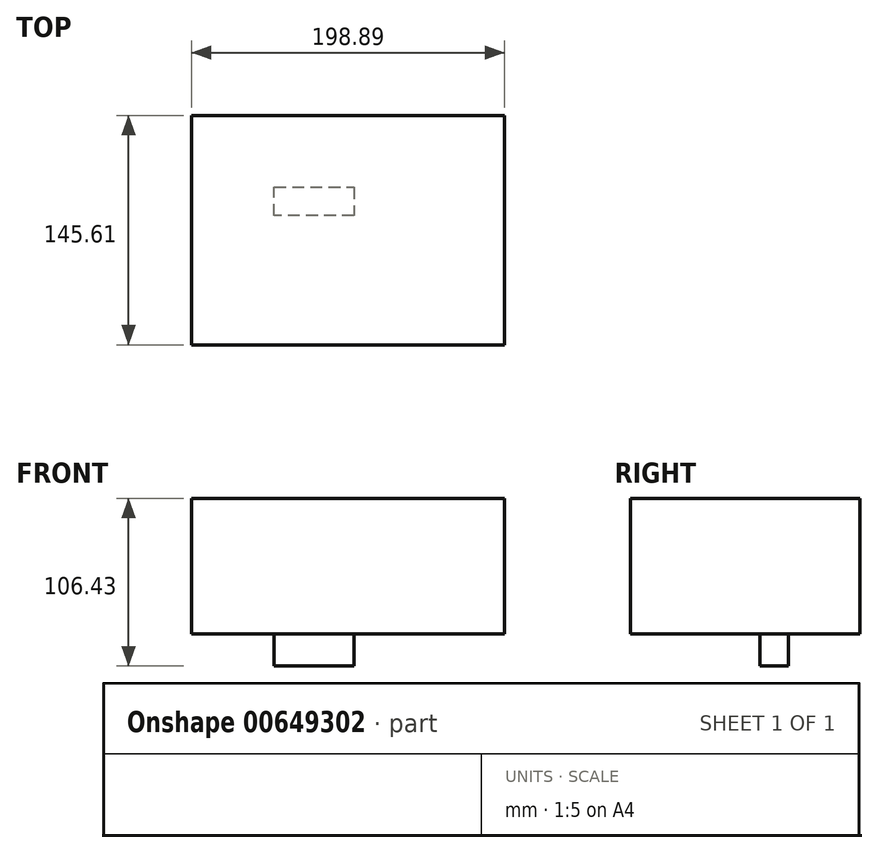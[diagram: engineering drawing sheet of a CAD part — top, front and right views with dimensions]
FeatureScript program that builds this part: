
annotation { "Feature Type Name" : "Feature", "Feature Type Description" : "" }
export const myFeature = defineFeature(function(context is Context, id is Id, definition is map)
    precondition{}
    {
        {
            var Q0;
            Q0=qCreatedBy(makeId("Top.planeOp"),FACE);
            var sketch = newSketch(context, id + "F0", { "sketchPlane" : qUnion([Q0])});
            skLineSegment(sketch, "E0.bottom", {"start": v(-103.24, 72.71) * mm, "end": v(95.65, 72.71) * mm});
            skLineSegment(sketch, "E0.top", {"start": v(-103.24, -72.9) * mm, "end": v(95.65, -72.9) * mm});
            skLineSegment(sketch, "E0.left", {"start": v(-103.24, 72.71) * mm, "end": v(-103.24, -72.9) * mm});
            skLineSegment(sketch, "E0.right", {"start": v(95.65, 72.71) * mm, "end": v(95.65, -72.9) * mm});
            skSolve(sketch);
        }
        {
            var Q0;
            Q0 = qSketchRegion(id + "F0", true);
            extrude(context, id + "F1", {"entities" : qUnion([Q0]), "depth" : 86.1 * mm, "offsetDistance" : 25.4 * mm});
        }
        {
            var Q0;
            Q0=qCreatedBy(makeId("Top.planeOp"),FACE);
            var sketch = newSketch(context, id + "F2", { "sketchPlane" : qUnion([Q0])});
            skLineSegment(sketch, "E1", {"start": v(19.62, 72.52) * mm, "end": v(19.62, 60.39) * mm});
            skLineSegment(sketch, "E2", {"start": v(19.62, 60.39) * mm, "end": v(39.53, 60.39) * mm});
            skLineSegment(sketch, "E3", {"start": v(39.53, 60.39) * mm, "end": v(39.53, 72.9) * mm});
            skLineSegment(sketch, "E4", {"start": v(39.53, 72.9) * mm, "end": v(39.53, 60.39) * mm});
            skLineSegment(sketch, "E5", {"start": v(19.62, 60.39) * mm, "end": v(-82.2, 60.39) * mm});
            skLineSegment(sketch, "E6", {"start": v(-82.2, 60.39) * mm, "end": v(-82.2, -30.8) * mm});
            skLineSegment(sketch, "E7", {"start": v(-82.2, -30.8) * mm, "end": v(-82.2, -47.5) * mm});
            skLineSegment(sketch, "E8", {"start": v(-82.2, -47.5) * mm, "end": v(-56.6, -47.5) * mm});
            skLineSegment(sketch, "E9", {"start": v(-56.6, -47.5) * mm, "end": v(-56.6, -33.46) * mm});
            skLineSegment(sketch, "E10", {"start": v(-56.6, -33.46) * mm, "end": v(-52.23, -33.46) * mm});
            skLineSegment(sketch, "E11", {"start": v(-52.23, -33.46) * mm, "end": v(-52.23, -68.35) * mm});
            skLineSegment(sketch, "E12", {"start": v(-52.23, -68.35) * mm, "end": v(91.3, -68.35) * mm});
            skLineSegment(sketch, "E13", {"start": v(91.3, -68.35) * mm, "end": v(91.3, 9.2) * mm});
            skLineSegment(sketch, "E14", {"start": v(91.3, 9.2) * mm, "end": v(-50.72, 9.2) * mm});
            skLineSegment(sketch, "E15", {"start": v(-50.72, 9.2) * mm, "end": v(-50.72, 27.2) * mm});
            skLineSegment(sketch, "E16", {"start": v(-50.72, 27.2) * mm, "end": v(0, 27.2) * mm});
            skLineSegment(sketch, "E17", {"start": v(0, 27.2) * mm, "end": v(0, 9.2) * mm});
            skSolve(sketch);
        }
        {
            var Q0;
            Q0 = qSketchRegion(id + "F2", true);
            extrude(context, id + "F3", {"entities" : qUnion([Q0]), "operationType" : NewBodyOperationType.ADD, "oppositeDirection" : true, "depth" : 20.32 * mm, "offsetDistance" : 25.4 * mm});
        }
    });
